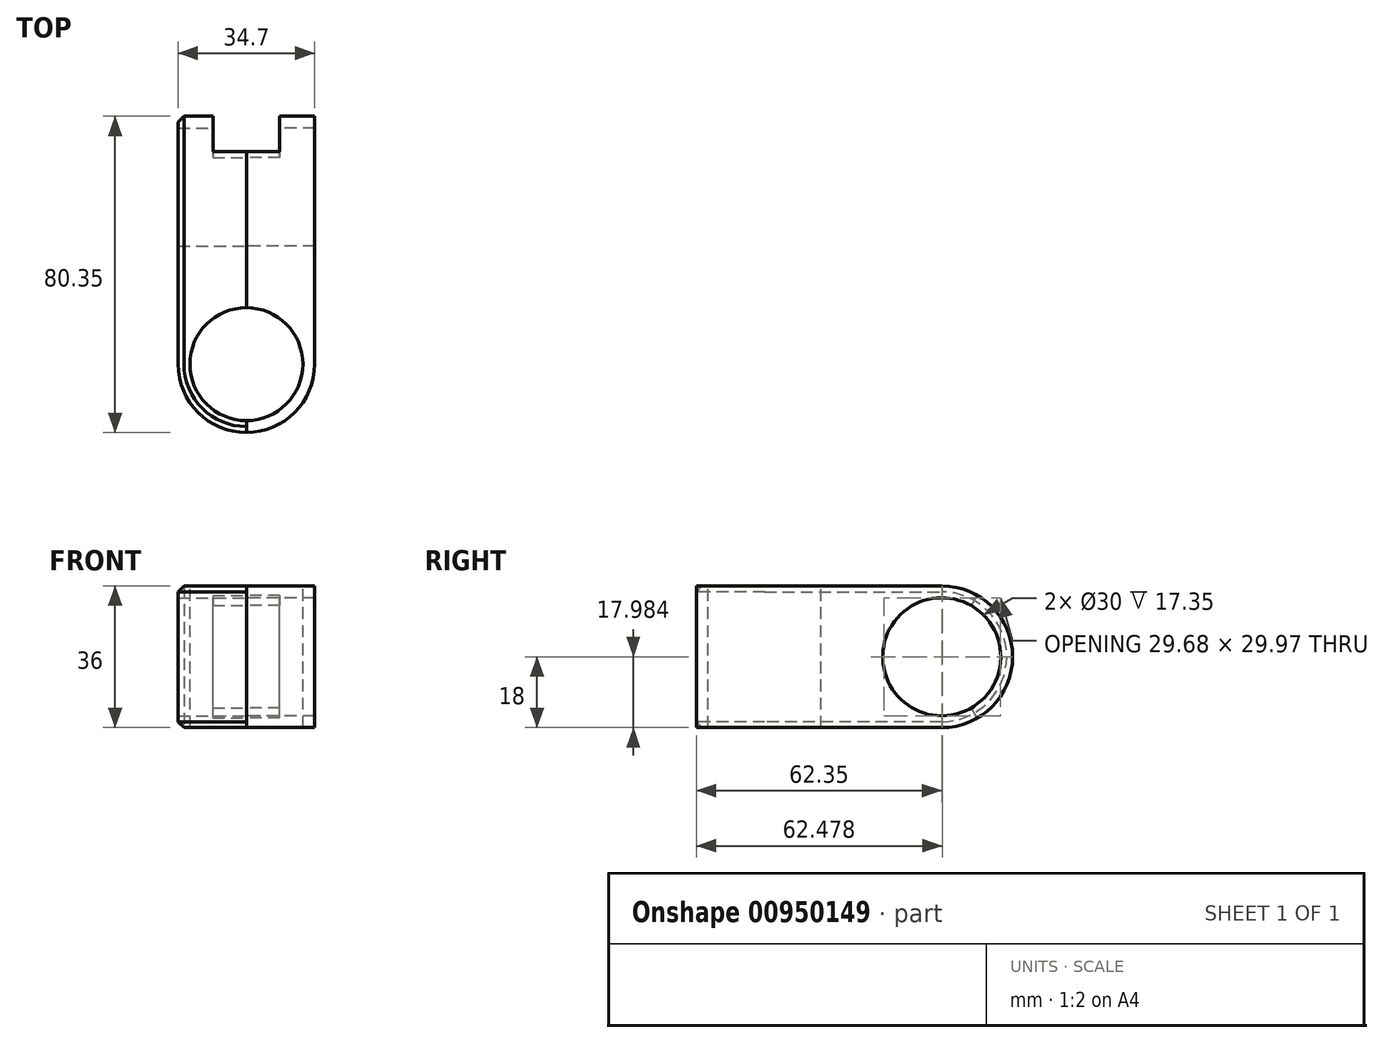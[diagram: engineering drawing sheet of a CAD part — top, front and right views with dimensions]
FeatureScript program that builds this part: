
annotation { "Feature Type Name" : "Feature", "Feature Type Description" : "" }
export const myFeature = defineFeature(function(context is Context, id is Id, definition is map)
    precondition{}
    {
        {
            var Q0;
            Q0=qCreatedBy(makeId("Right.planeOp"),FACE);
            var sketch = newSketch(context, id + "F0", { "sketchPlane" : qUnion([Q0])});
            skLineSegment(sketch, "E0", {"start": v(0, -18) * mm, "end": v(0, 18) * mm});
            skCircle(sketch, "E1", {"center": v(45, 0) * mm, "radius": 15 * mm});
            skArc(sketch, "E2", {"start": v(45, 18) * mm, "mid": v(63, 0) * mm, "end": v(45, -18) * mm});
            skLineSegment(sketch, "E3", {"start": v(-14.35, -18) * mm, "end": v(-14.35, 18) * mm});
            skLineSegment(sketch, "E4", {"start": v(-17.35, -18) * mm, "end": v(-17.35, 18) * mm});
            skLineSegment(sketch, "E5", {"start": v(-17.35, 18) * mm, "end": v(45, 18) * mm});
            skLineSegment(sketch, "E6", {"start": v(-17.35, -18) * mm, "end": v(45, -18) * mm});
            skLineSegment(sketch, "E7", {"start": v(54, 15.59) * mm, "end": v(52.5, 13) * mm});
            skLineSegment(sketch, "E8.MirrorCS", {"start": v(54, -15.59) * mm, "end": v(52.5, -13) * mm});
            skSolve(sketch);
        }
        {
            var Q0;
            Q0=qCreatedBy(makeId("Top.planeOp"),FACE);
            var sketch = newSketch(context, id + "F1", { "sketchPlane" : qUnion([Q0])});
            skArc(sketch, "E9", {"start": v(305, 5.58) * mm, "mid": v(153.8, 35.53) * mm, "end": v(0, 45.58) * mm});
            skSolve(sketch);
        }
        {
            var Q0;
            Q0=sQuery(id+"F1.wireOp",EDGE,"E9");
            cPlane(context, id + "F2", {"entities" : qUnion([Q0]), "cplaneType" : CPlaneType.MID_PLANE, "offset" : 25 * mm, "oppositeDirection" : true, "width" : 150 * mm, "height" : 150 * mm});
        }
        {
            var Q0;
            Q0=sQuery(id+"F1.wireOp",EDGE,"E9");
            var Q1;
            Q1=sQuery(id+"F1.wireOp",VERTEX,"E9.start");
            cPlane(context, id + "F3", {"entities" : qUnion([Q0, Q1]), "cplaneType" : CPlaneType.CURVE_POINT, "offset" : 25 * mm, "width" : 150 * mm, "height" : 150 * mm});
        }
        {
            var Q0;
            Q0=qCreatedBy(id+"F2.planeOp",FACE);
            var sketch = newSketch(context, id + "F4", { "sketchPlane" : qUnion([Q0])});
            skCircle(sketch, "E10", {"center": v(-55.23, 0) * mm, "radius": 11 * mm});
            skSolve(sketch);
        }
        {
            var Q0;
            Q0=qCreatedBy(id+"F3.planeOp",FACE);
            var sketch = newSketch(context, id + "F5", { "sketchPlane" : qUnion([Q0])});
            skCircle(sketch, "E11", {"center": v(-84.04, 0) * mm, "radius": 11 * mm});
            skSolve(sketch);
        }
        {
            var Q0;
            Q0=makeQuery(id+"F0.imprint","IMPRINT",FACE,{"disambiguationData":[TD([[makeQuery(id+"F0.imprint","IMPRINT",EDGE,{"derivedFrom":sQuery(id+"F0.wireOp",EDGE,"E1")}),1.0]])]});
            var Q1;
            Q1=makeQuery(id+"F4.imprint","IMPRINT",FACE,{"disambiguationData":[TD([[makeQuery(id+"F4.imprint","IMPRINT",EDGE,{"derivedFrom":sQuery(id+"F4.wireOp",EDGE,"E10")}),1.0]])]});
            var Q2;
            Q2=makeQuery(id+"F5.imprint","IMPRINT",FACE,{"disambiguationData":[TD([[makeQuery(id+"F5.imprint","IMPRINT",EDGE,{"derivedFrom":sQuery(id+"F5.wireOp",EDGE,"E11")}),1.0]])]});
            loft(context, id + "F6", {"startCondition" : LoftEndDerivativeType.NORMAL_TO_PROFILE, "startMagnitude" : 1.8, "sheetProfilesArray" : [{ "sheetProfileEntities" : qUnion([Q0]) }, { "sheetProfileEntities" : qUnion([Q1]) }, { "sheetProfileEntities" : qUnion([Q2]) }]});
        }
        {
            var Q0;
            Q0=makeQuery(id+"F6.opLoft","SWEPT_BODY",BODY,{"disambiguationData":[OSD([makeQuery(id+"F0.imprint","IMPRINT",FACE,{"disambiguationData":[TD([[makeQuery(id+"F0.imprint","IMPRINT",EDGE,{"derivedFrom":sQuery(id+"F0.wireOp",EDGE,"E1")}),1.0]])]}),sQuery(id+"F4.wireOp",EDGE,"E10"),makeQuery(id+"F5.imprint","IMPRINT",FACE,{"disambiguationData":[TD([[makeQuery(id+"F5.imprint","IMPRINT",EDGE,{"derivedFrom":sQuery(id+"F5.wireOp",EDGE,"E11")}),1.0]])]})])]});
            var Q1;
            Q1=makeQuery(id+"F6.opLoft","CAP_FACE",FACE,{"disambiguationData":[OSD([makeQuery(id+"F0.imprint","IMPRINT",FACE,{"disambiguationData":[TD([[makeQuery(id+"F0.imprint","IMPRINT",EDGE,{"derivedFrom":sQuery(id+"F0.wireOp",EDGE,"E1")}),1.0]])]})])],"isStart":true});
            mirror(context, id + "F7", {"operationType" : NewBodyOperationType.ADD, "entities" : qUnion([Q0]), "mirrorPlane" : qUnion([Q1])});
        }
        {
            var Q0;
            {var subQ0=sQuery(id+"F0.wireOp",EDGE,"E0");Q0=makeQuery(id+"F0.imprint","IMPRINT",FACE,{"disambiguationData":[TD([[makeQuery(id+"F0.imprint","IMPRINT",EDGE,{"derivedFrom":subQ0}),1.0]])]});}
            var Q1;
            {var subQ0=sQuery(id+"F0.wireOp",EDGE,"E3");Q1=makeQuery(id+"F0.imprint","IMPRINT",FACE,{"disambiguationData":[TD([[makeQuery(id+"F0.imprint","IMPRINT",EDGE,{"derivedFrom":subQ0}),1.0]])]});}
            var Q2;
            Q2=sQuery(id+"F0.wireOp",EDGE,"E0");
            revolve(context, id + "F8", {"surfaceOperationType" : NewSurfaceOperationType.NEW, "entities" : qUnion([Q0, Q1]), "axis" : qUnion([Q2]), "revolveType" : RevolveType.ONE_DIRECTION, "angle" : 90 * degree});
        }
        {
            var Q0;
            {var subQ1=sQuery(id+"F0.wireOp",EDGE,"E0");Q0=makeQuery(id+"F0.imprint","IMPRINT",FACE,{"disambiguationData":[TD([[makeQuery(id+"F0.imprint","IMPRINT",EDGE,{"derivedFrom":subQ1}),-1.0]])]});}
            var Q1;
            {var subQ0=sQuery(id+"F0.wireOp",EDGE,"E7");Q1=makeQuery(id+"F0.imprint","IMPRINT",FACE,{"disambiguationData":[TD([[makeQuery(id+"F0.imprint","IMPRINT",EDGE,{"derivedFrom":subQ0}),1.0]])]});}
            var Q2;
            Q2=makeQuery(id+"F8.opRevolve","CAP_VERTEX",VERTEX,{"disambiguationData":[OSD([sQuery(id+"F0.wireOp",EDGE,"E4"),sQuery(id+"F0.wireOp",EDGE,"E5")])],"isStart":false});
            extrude(context, id + "F9", {"entities" : qUnion([Q0, Q1]), "operationType" : NewBodyOperationType.ADD, "endBound" : BoundingType.UP_TO_VERTEX, "depth" : 25 * mm, "endBoundEntityVertex" : qUnion([Q2]), "offsetDistance" : 25 * mm});
        }
        {
            var Q0;
            {var subQ0=sQuery(id+"F0.wireOp",EDGE,"E7");Q0=makeQuery(id+"F0.imprint","IMPRINT",FACE,{"disambiguationData":[TD([[makeQuery(id+"F0.imprint","IMPRINT",EDGE,{"derivedFrom":subQ0}),1.0]])]});}
            extrude(context, id + "F10", {"entities" : qUnion([Q0]), "operationType" : NewBodyOperationType.REMOVE, "depth" : 8.5 * mm, "offsetDistance" : 25 * mm});
        }
        {
            var Q0;
            {var subQ0=sQuery(id+"F0.wireOp",EDGE,"E0");Q0=makeQuery(id+"F0.imprint","IMPRINT",FACE,{"disambiguationData":[TD([[makeQuery(id+"F0.imprint","IMPRINT",EDGE,{"derivedFrom":subQ0}),1.0]])]});}
            var Q1;
            Q1=sQuery(id+"F0.wireOp",EDGE,"E0");
            revolve(context, id + "F11", {"operationType" : NewBodyOperationType.REMOVE, "surfaceOperationType" : NewSurfaceOperationType.NEW, "entities" : qUnion([Q0]), "axis" : qUnion([Q1]), "revolveType" : RevolveType.FULL, "oppositeDirection" : true});
        }
        {
            var Q0;
            Q0=makeQuery(id+"F8.opRevolve","SWEPT_BODY",BODY,{"disambiguationData":[OSD([sQuery(id+"F0.wireOp",EDGE,"E0"),sQuery(id+"F0.wireOp",EDGE,"E4"),sQuery(id+"F0.wireOp",EDGE,"E5"),sQuery(id+"F0.wireOp",EDGE,"E6")])]});
            var Q1;
            {var subQ1=sQuery(id+"F0.wireOp",EDGE,"E0");Q1=makeQuery(id+"F0.imprint","IMPRINT",FACE,{"disambiguationData":[TD([[makeQuery(id+"F0.imprint","IMPRINT",EDGE,{"derivedFrom":subQ1}),-1.0]])]});}
            mirror(context, id + "F12", {"operationType" : NewBodyOperationType.ADD, "entities" : qUnion([Q0]), "mirrorPlane" : qUnion([Q1])});
        }
        {
            var Q0;
            Q0=makeQuery(id+"F12.opPattern","COPY",EDGE,{"derivedFrom":makeQuery(id+"F9.opExtrude","CAP_EDGE",EDGE,{"disambiguationData":[OSD([sQuery(id+"F0.wireOp",EDGE,"E5")])],"isStart":false}),"instanceName":"1"});
            var Q1;
            Q1=makeQuery(id+"F10.boolean.opBoolean","COPY",EDGE,{"derivedFrom":makeQuery(id+"F10.opExtrude","CAP_EDGE",EDGE,{"disambiguationData":[OSD([sQuery(id+"F0.wireOp",EDGE,"E2")])],"isStart":false})});
            var Q2;
            Q2=makeQuery(id+"F12.opPattern","COPY",EDGE,{"derivedFrom":makeQuery(id+"F10.boolean.opBoolean","COPY",EDGE,{"derivedFrom":makeQuery(id+"F10.opExtrude","CAP_EDGE",EDGE,{"disambiguationData":[OSD([sQuery(id+"F0.wireOp",EDGE,"E2")])],"isStart":false})}),"instanceName":"1"});
            var Q3;
            {var subQ0=makeQuery(id+"F10.boolean.opBoolean","COPY",EDGE,{"derivedFrom":makeQuery(id+"F10.opExtrude","SWEPT_EDGE",EDGE,{"disambiguationData":[OSD([sQuery(id+"F0.wireOp",EDGE,"E2"),sQuery(id+"F0.wireOp",EDGE,"E7")])]})});Q3=makeQuery(id+"F12.boolean.opBoolean","MERGE",EDGE,{"derivedFrom":[subQ0,makeQuery(id+"F12.opPattern","COPY",EDGE,{"derivedFrom":subQ0,"instanceName":"1"})]});}
            var Q4;
            {var subQ0=makeQuery(id+"F10.boolean.opBoolean","COPY",EDGE,{"derivedFrom":makeQuery(id+"F10.opExtrude","SWEPT_EDGE",EDGE,{"disambiguationData":[OSD([sQuery(id+"F0.wireOp",EDGE,"E2"),sQuery(id+"F0.wireOp",EDGE,"E8.MirrorCS")])]})});Q4=makeQuery(id+"F12.boolean.opBoolean","MERGE",EDGE,{"derivedFrom":[subQ0,makeQuery(id+"F12.opPattern","COPY",EDGE,{"derivedFrom":subQ0,"instanceName":"1"})]});}
            chamfer(context, id + "F13", {"entities" : qUnion([Q0, Q1, Q2, Q3, Q4]), "width" : 1.5 * mm, "tangentPropagation" : true});
        }
    });
